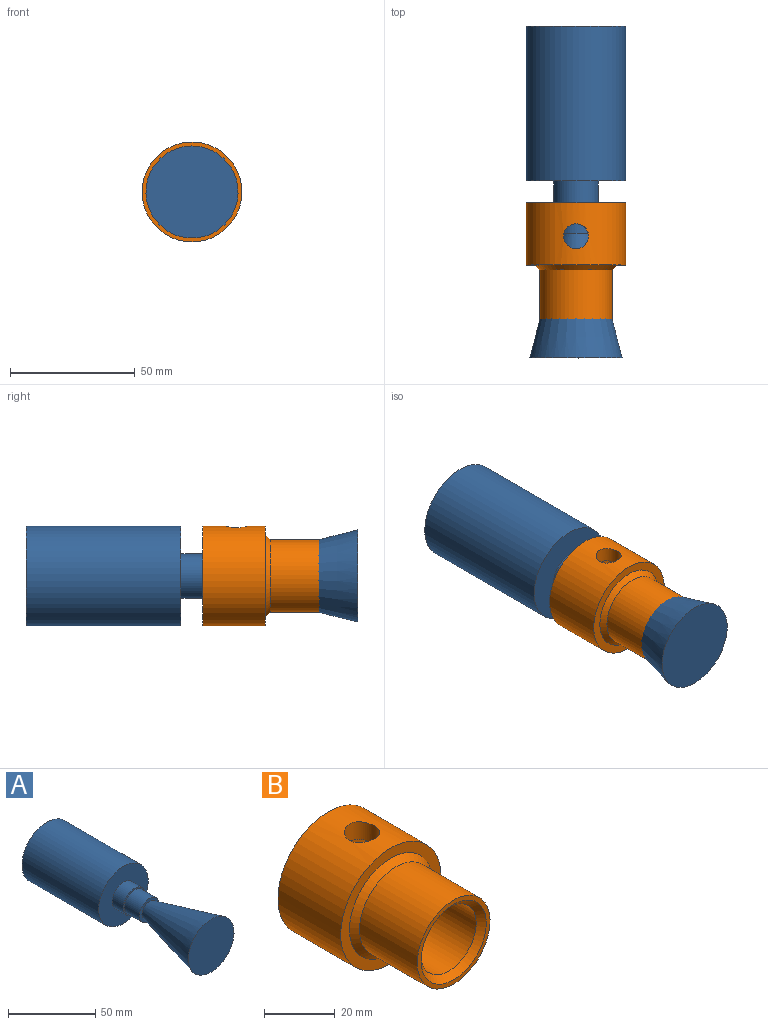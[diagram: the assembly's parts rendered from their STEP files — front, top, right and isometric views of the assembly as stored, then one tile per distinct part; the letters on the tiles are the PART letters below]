
ASSEMBLY  parts=2 mates=1
PART A: 9 faces, bbox 40x132.9x40 mm
  f0: cylinder r=20mm len=62mm, axis (0,1,0), area 7791.1mm2, adj f1,f2
  f1: plane 40x40mm, normal (0,-1,0), area 1002.2mm2, adj f0,f3
  f2: plane 40x40mm, normal (0,1,0), area 1256.6mm2, adj f0
  f3: cylinder r=9mm len=18mm, axis (0,1,0), area 497.6mm2, adj f1,f4
  f4: plane 18x18mm, normal (0,-1,0), area 53.4mm2, adj f3,f5
  f5: cylinder r=8mm len=16mm, axis (0,1,0), area 610.2mm2, adj f4,f6
  f6: plane 16x16mm, normal (0,-1,0), area 89.8mm2, adj f5,f7
  f7: cone r=18.45mm half-angle=14deg, axis (0,-1,0), area 3950.7mm2, adj f6,f8
  f8: plane 36.9x36.9mm, normal (0,-1,0), area 1069.4mm2, adj f7
PART B: 13 faces, bbox 40x50x40 mm
  f0: cylinder r=14mm len=28mm, axis (0,-1,0), area 1653.3mm2, adj f2,f9,f11
  f1: cylinder r=20mm len=40mm, axis (0,-1,0), area 3062.6mm2, adj f6,f7,f11
  f2: plane 28x28mm, normal (0,1,0), area 235.6mm2, adj f0,f3
  f3: cylinder r=11mm len=23mm, axis (0,1,0), area 1589.6mm2, adj f2,f12
  f4: cylinder r=14.5mm len=29mm, axis (0,1,0), area 2095.4mm2, adj f5,f8
  f5: plane 29x29mm, normal (0,-1,0), area 129.6mm2, adj f4,f12
  f6: plane 40x40mm, normal (0,-1,0), area 401.3mm2, adj f1,f8
  f7: plane 40x40mm, normal (0,1,0), area 1079.9mm2, adj f1,f10
  f8: cone r=14.5mm half-angle=45deg, axis (0,1,0), area 275.5mm2, adj f4,f6
  f9: plane 28x28mm, normal (0,-1,0), area 439mm2, adj f0,f10
  f10: cylinder r=7.5mm len=15mm, axis (0,1,0), area 249.8mm2, adj f7,f9
  f11: cylinder r=5mm len=10mm, axis (0,0,-1), area 193mm2, adj f0,f1
  f12: cone r=11mm half-angle=45deg, axis (0,-1,0), area 213.3mm2, adj f3,f5
PLACE A rot(axis=(-0.04,-0.09,-0.99),0deg) t=(-14.56,-3.54,-6.64)mm fixed
PLACE B rot(axis=(-0.04,-0.09,-0.99),0deg) t=(-14.56,-99.26,-6.64)mm
MATE slider B.f10 <-> A.f5  axis (0,1,0) through (-14.56,-74.26,-6.64)mm
